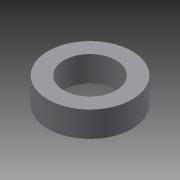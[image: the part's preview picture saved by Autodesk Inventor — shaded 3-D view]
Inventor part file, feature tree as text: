
AUTODESK INVENTOR PART (.ipt)
format: ipt  version: 2013 (Build 170138000, 138)  size: 73,728 bytes
history: native  units: mm
features: extrude x1, sketch x1
ambient origin geometry x8: Origin, YZ Plane, XZ Plane, XY Plane, X Axis, Y Axis, Z Axis, Center Point
bodies: Solid1 (feature_tree)
feature tree (2):
  extrude  "Extrusion1"  Depth=2.5mm
  sketch  "Sketch1"  dims[d0=8.2mm d2=2.5mm d3=4.0mm d4=0.0mm]
